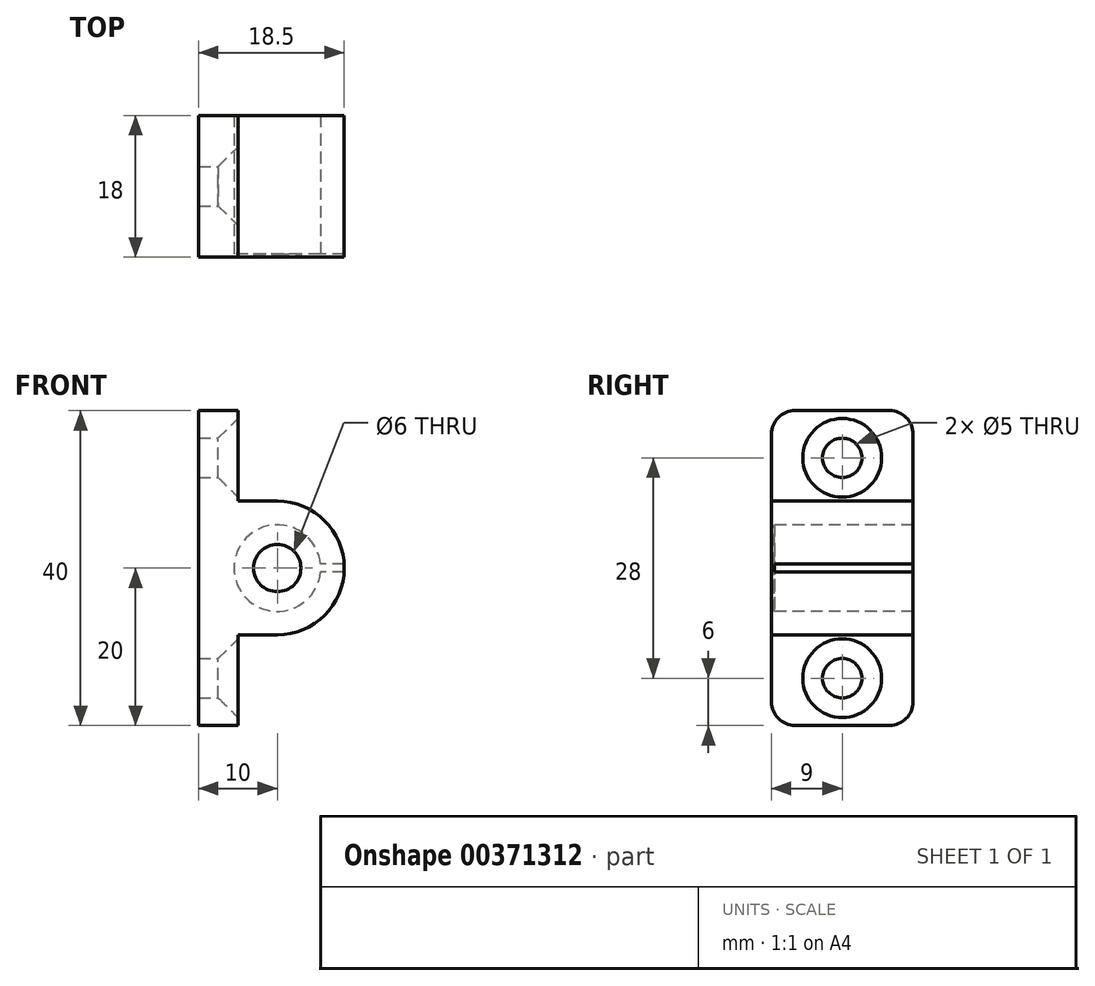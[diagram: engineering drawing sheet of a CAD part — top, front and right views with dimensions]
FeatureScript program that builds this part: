
annotation { "Feature Type Name" : "Feature", "Feature Type Description" : "" }
export const myFeature = defineFeature(function(context is Context, id is Id, definition is map)
    precondition{}
    {
        {
            var Q0;
            Q0=qCreatedBy(makeId("Front.planeOp"),FACE);
            var sketch = newSketch(context, id + "F0", { "sketchPlane" : qUnion([Q0])});
            skCircle(sketch, "E0", {"center": v(0, 0) * mm, "radius": 8.5 * mm});
            skLineSegment(sketch, "E1.bottom", {"start": v(-10, -20) * mm, "end": v(-5, -20) * mm});
            skLineSegment(sketch, "E1.top", {"start": v(-10, 20) * mm, "end": v(-5, 20) * mm});
            skLineSegment(sketch, "E1.left", {"start": v(-10, -20) * mm, "end": v(-10, 20) * mm});
            skLineSegment(sketch, "E1.right", {"start": v(-5, -20) * mm, "end": v(-5, 20) * mm});
            skLineSegment(sketch, "E2", {"start": v(0, 8.5) * mm, "end": v(-5, 8.5) * mm});
            skLineSegment(sketch, "E3", {"start": v(0, -8.5) * mm, "end": v(-5, -8.5) * mm});
            skSolve(sketch);
        }
        {
            var Q0;
            {var subQ1=sQuery(id+"F0.wireOp",EDGE,"E1.bottom");Q0=makeQuery(id+"F0.imprint","IMPRINT",FACE,{"disambiguationData":[TD([[makeQuery(id+"F0.imprint","IMPRINT",EDGE,{"derivedFrom":subQ1}),1.0]])]});}
            var Q1;
            {var subQ0=sQuery(id+"F0.wireOp",EDGE,"E0");var subQ1=makeQuery(id+"F0.imprint","INTERSECT",VERTEX,{"derivedFrom":[subQ0,sQuery(id+"F0.wireOp",EDGE,"E2")]});Q1=makeQuery(id+"F0.imprint","IMPRINT",FACE,{"disambiguationData":[TD([[makeQuery(id+"F0.imprint","IMPRINT",EDGE,{"disambiguationData":[TD([[subQ1,-1.0]])],"derivedFrom":subQ0}),1.0]])]});}
            var Q2;
            {var subQ0=sQuery(id+"F0.wireOp",EDGE,"E3");Q2=makeQuery(id+"F0.imprint","IMPRINT",FACE,{"disambiguationData":[TD([[makeQuery(id+"F0.imprint","IMPRINT",EDGE,{"derivedFrom":subQ0}),-1.0]])]});}
            var Q3;
            {var subQ0=sQuery(id+"F0.wireOp",EDGE,"E1.right");var subQ1=sQuery(id+"F0.wireOp",EDGE,"E0");var subQ2=makeQuery(id+"F0.imprint","INTERSECT",VERTEX,{"disambiguationData":[OD(0.0)],"derivedFrom":[subQ1,subQ0]});Q3=makeQuery(id+"F0.imprint","IMPRINT",FACE,{"disambiguationData":[TD([[makeQuery(id+"F0.imprint","IMPRINT",EDGE,{"disambiguationData":[TD([[subQ2,-1.0]])],"derivedFrom":subQ1}),1.0]])]});}
            var Q4;
            {var subQ0=sQuery(id+"F0.wireOp",EDGE,"E2");Q4=makeQuery(id+"F0.imprint","IMPRINT",FACE,{"disambiguationData":[TD([[makeQuery(id+"F0.imprint","IMPRINT",EDGE,{"derivedFrom":subQ0}),1.0]])]});}
            extrude(context, id + "F1", {"entities" : qUnion([Q0, Q1, Q2, Q3, Q4]), "depth" : 18 * mm});
        }
        {
            var Q0;
            Q0=makeQuery(id+"F1.opExtrude","CAP_FACE",FACE,{"disambiguationData":[OSD([sQuery(id+"F0.wireOp",EDGE,"E0"),sQuery(id+"F0.wireOp",EDGE,"E1.bottom"),sQuery(id+"F0.wireOp",EDGE,"E1.top"),sQuery(id+"F0.wireOp",EDGE,"E1.left"),sQuery(id+"F0.wireOp",EDGE,"E1.right"),sQuery(id+"F0.wireOp",EDGE,"E2"),sQuery(id+"F0.wireOp",EDGE,"E3")])],"isStart":false});
            var sketch = newSketch(context, id + "F2", { "sketchPlane" : qUnion([Q0])});
            skCircle(sketch, "E4", {"center": v(0, 0) * mm, "radius": 5.5 * mm});
            skSolve(sketch);
        }
        {
            var Q0;
            Q0 = qSketchRegion(id + "F2", true);
            extrude(context, id + "F3", {"entities" : qUnion([Q0]), "operationType" : NewBodyOperationType.REMOVE, "endBound" : BoundingType.UP_TO_NEXT, "oppositeDirection" : true, "depth" : 17 * mm});
        }
        {
            var Q0;
            {var subQ0=sQuery(id+"F0.wireOp",EDGE,"E1.right");Q0=makeQuery(id+"F1.opExtrude","SWEPT_FACE",FACE,{"disambiguationData":[OSD([subQ0]),TDD([makeQuery(id+"F0.imprint","IMPRINT",EDGE,{"disambiguationData":[TD([[makeQuery(id+"F0.imprint","INTERSECT",VERTEX,{"derivedFrom":[sQuery(id+"F0.wireOp",EDGE,"E1.bottom"),subQ0]}),-1.0]])],"derivedFrom":subQ0})])]});}
            var sketch = newSketch(context, id + "F4", { "sketchPlane" : qUnion([Q0])});
            skLineSegment(sketch, "E5", {"start": v(-9, -20) * mm, "end": v(-9, 20) * mm, "construction": true});
            skPoint(sketch, "E6", {"position": v(-9, -14) * mm});
            skPoint(sketch, "E7.MirrorP", {"position": v(-9, 14) * mm});
            skSolve(sketch);
        }
        {
            var Q0;
            Q0=sQuery(id+"F4.wireOp",VERTEX,"E6");
            var Q1;
            Q1=sQuery(id+"F4.wireOp",VERTEX,"E7.MirrorP");
            var Q2;
            Q2=makeQuery(id+"F1.opExtrude","SWEPT_BODY",BODY,{"disambiguationData":[OSD([sQuery(id+"F0.wireOp",EDGE,"E0"),sQuery(id+"F0.wireOp",EDGE,"E1.bottom"),sQuery(id+"F0.wireOp",EDGE,"E1.top"),sQuery(id+"F0.wireOp",EDGE,"E1.left"),sQuery(id+"F0.wireOp",EDGE,"E1.right"),sQuery(id+"F0.wireOp",EDGE,"E2"),sQuery(id+"F0.wireOp",EDGE,"E3")])]});
            hole(context, id + "F5", {"style" : HoleStyle.C_SINK, "endStyle" : HoleEndStyle.THROUGH, "holeDiameter" : 5 * mm, "cSinkDiameter" : 10 * mm, "cSinkAngle" : 90 * degree, "isTappedThrough" : true, "tappedDepth" : 12 * mm, "tapClearance" : 3, "locations" : qUnion([Q0, Q1]), "scope" : qUnion([Q2])});
        }
        {
            var Q0;
            Q0=qCreatedBy(makeId("Front.planeOp"),FACE);
            var sketch = newSketch(context, id + "F6", { "sketchPlane" : qUnion([Q0])});
            skLineSegment(sketch, "E8.bottom", {"start": v(10.78, -0.5) * mm, "end": v(3.43, -0.5) * mm});
            skLineSegment(sketch, "E8.top", {"start": v(10.78, 0.5) * mm, "end": v(3.43, 0.5) * mm});
            skLineSegment(sketch, "E8.left", {"start": v(10.78, -0.5) * mm, "end": v(10.78, 0.5) * mm});
            skLineSegment(sketch, "E8.right", {"start": v(3.43, -0.5) * mm, "end": v(3.43, 0.5) * mm});
            skPoint(sketch, "E8.middle", {"position": v(7.1, 0) * mm});
            skSolve(sketch);
        }
        {
            var Q0;
            Q0 = qSketchRegion(id + "F6", true);
            extrude(context, id + "F7", {"entities" : qUnion([Q0]), "operationType" : NewBodyOperationType.REMOVE, "endBound" : BoundingType.UP_TO_NEXT, "depth" : 25 * mm});
        }
        {
            var Q0;
            Q0=makeQuery(id+"F1.opExtrude","CAP_EDGE",EDGE,{"disambiguationData":[OSD([sQuery(id+"F0.wireOp",EDGE,"E1.bottom")])],"isStart":false});
            var Q1;
            Q1=makeQuery(id+"F1.opExtrude","CAP_EDGE",EDGE,{"disambiguationData":[OSD([sQuery(id+"F0.wireOp",EDGE,"E1.top")])],"isStart":false});
            var Q2;
            Q2=makeQuery(id+"F1.opExtrude","CAP_EDGE",EDGE,{"disambiguationData":[OSD([sQuery(id+"F0.wireOp",EDGE,"E1.top")])],"isStart":true});
            var Q3;
            Q3=makeQuery(id+"F1.opExtrude","CAP_EDGE",EDGE,{"disambiguationData":[OSD([sQuery(id+"F0.wireOp",EDGE,"E1.bottom")])],"isStart":true});
            fillet(context, id + "F8", {"entities" : qUnion([Q0, Q1, Q2, Q3]), "radius" : 3 * mm, "tangentPropagation" : true, "allowEdgeOverflow" : false});
        }
        {
            var Q0;
            Q0=makeQuery(id+"F1.opExtrude","CAP_FACE",FACE,{"disambiguationData":[OSD([sQuery(id+"F0.wireOp",EDGE,"E0"),sQuery(id+"F0.wireOp",EDGE,"E1.bottom"),sQuery(id+"F0.wireOp",EDGE,"E1.top"),sQuery(id+"F0.wireOp",EDGE,"E1.left"),sQuery(id+"F0.wireOp",EDGE,"E1.right"),sQuery(id+"F0.wireOp",EDGE,"E2"),sQuery(id+"F0.wireOp",EDGE,"E3")])],"isStart":false});
            var sketch = newSketch(context, id + "F9", { "sketchPlane" : qUnion([Q0])});
            skCircle(sketch, "E9", {"center": v(0, 0) * mm, "radius": 8.5 * mm});
            skCircle(sketch, "E10", {"center": v(0, 0) * mm, "radius": 3 * mm});
            skSolve(sketch);
        }
        {
            var Q0;
            Q0 = qSketchRegion(id + "F9", true);
            extrude(context, id + "F10", {"entities" : qUnion([Q0]), "operationType" : NewBodyOperationType.ADD, "oppositeDirection" : true, "depth" : .4 * mm});
        }
    });
